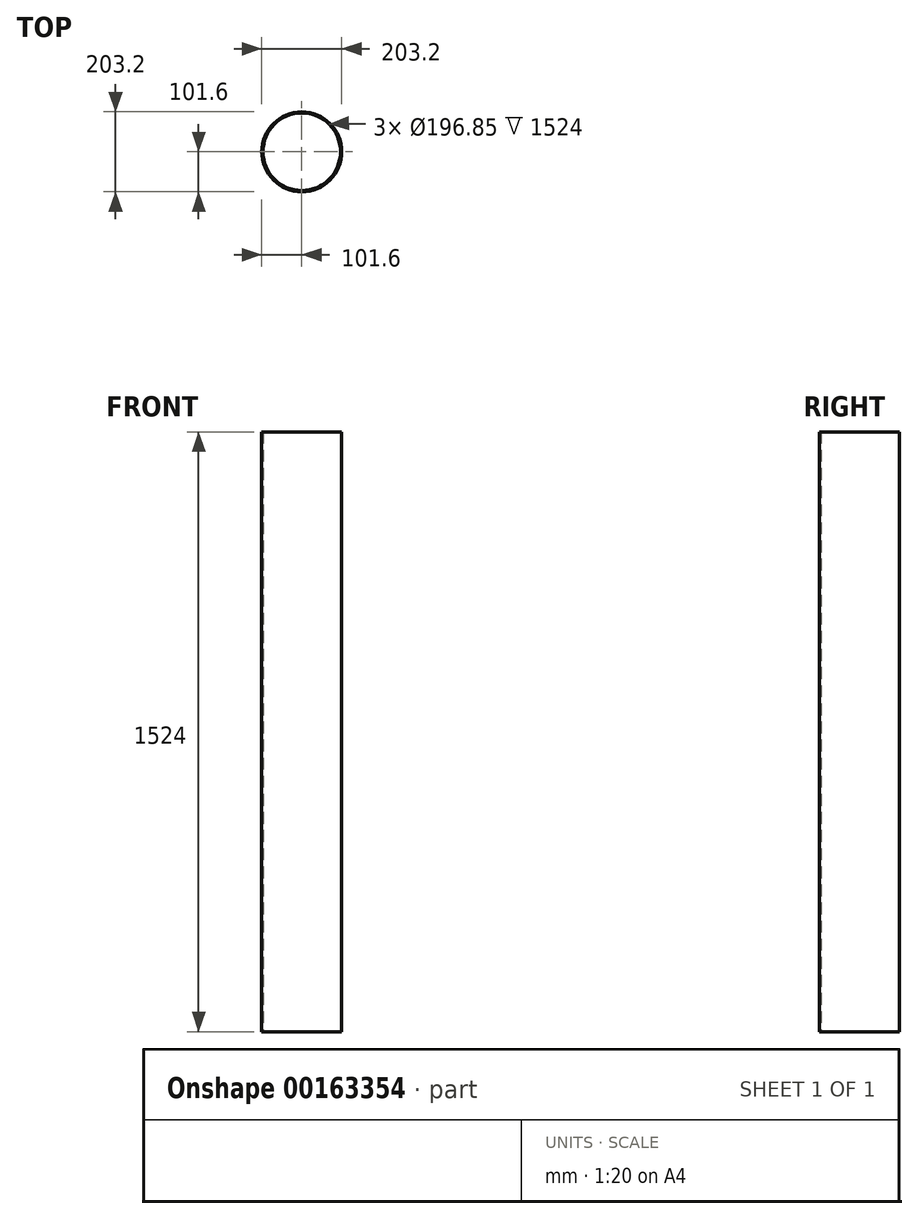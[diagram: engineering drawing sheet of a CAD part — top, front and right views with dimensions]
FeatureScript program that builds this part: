
annotation { "Feature Type Name" : "Feature", "Feature Type Description" : "" }
export const myFeature = defineFeature(function(context is Context, id is Id, definition is map)
    precondition{}
    {
        {
            var Q0;
            Q0=qCreatedBy(makeId("Top.planeOp"),FACE);
            var sketch = newSketch(context, id + "F0", { "sketchPlane" : qUnion([Q0])});
            skCircle(sketch, "E0", {"center": v(0, 0) * mm, "radius": 101.6 * mm});
            skCircle(sketch, "E1", {"center": v(0, 0) * mm, "radius": 98.43 * mm});
            skSolve(sketch);
        }
        {
            var Q0;
            Q0=makeQuery(id+"F0.imprint","IMPRINT",FACE,{"disambiguationData":[TD([[makeQuery(id+"F0.imprint","IMPRINT",EDGE,{"derivedFrom":sQuery(id+"F0.wireOp",EDGE,"E0")}),1.0]])]});
            extrude(context, id + "F1", {"entities" : qUnion([Q0]), "endBound" : BoundingType.SYMMETRIC, "depth" : 1524 * mm});
        }
    });
